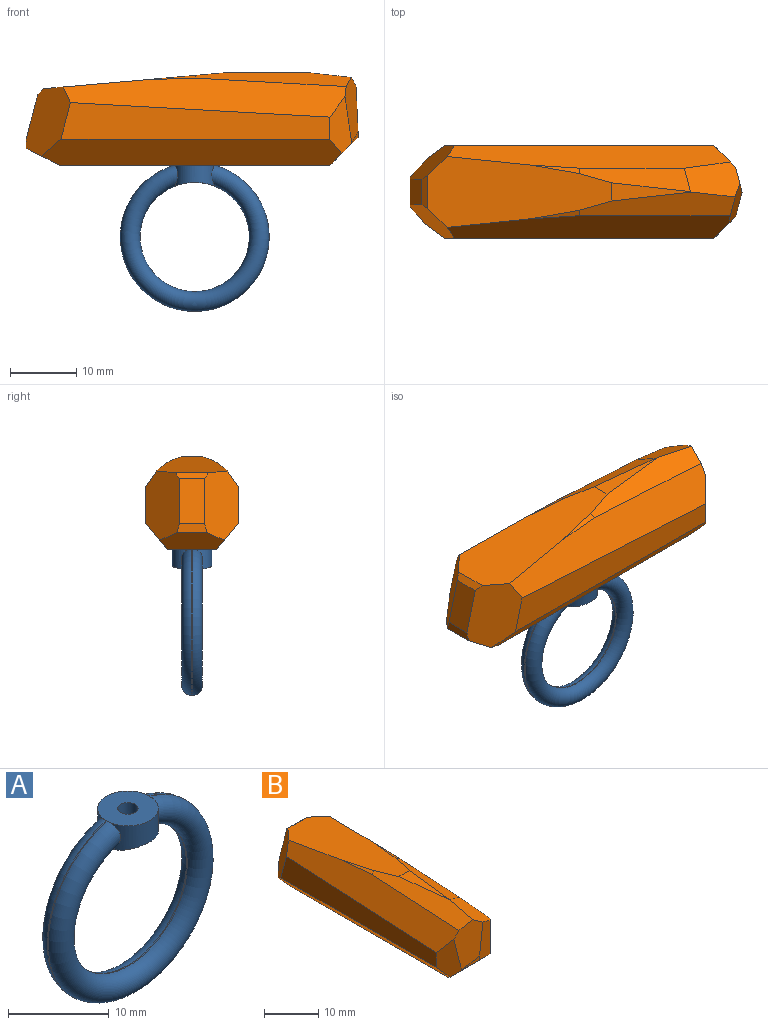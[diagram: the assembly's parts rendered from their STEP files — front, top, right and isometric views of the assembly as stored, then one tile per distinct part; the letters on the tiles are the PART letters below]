
ASSEMBLY  parts=2 mates=1
PART A: 8 faces, bbox 24.4x6x24 mm
  f0: cylinder r=11.25mm len=22.5mm, axis (0,1,0), area 7.9mm2, adj f1,f2,f4,f5,f6
  f1: cylinder r=3mm len=6mm, axis (0,0,-1), area 19mm2, adj f0,f3,f4,f6
  f2: cylinder r=3mm len=6mm, axis (0,0,-1), area 19mm2, adj f0,f3,f5,f6
  f3: cylinder r=8.25mm len=16.5mm, axis (0,1,0), area 31.2mm2, adj f1,f2,f4,f5,f7
  f4: torus R=9.75mm, axis (0,1,0), area 262.1mm2, adj f0,f1,f3
  f5: torus R=9.75mm, axis (0,1,0), area 262.1mm2, adj f0,f2,f3
  f6: plane 6x5.98mm, normal (0,0,1), area 25.1mm2, adj f0,f1,f2,f7
  f7: cylinder r=1mm len=2.66mm, axis (0,0,1), area 16.5mm2, adj f3,f6
PART B: 26 faces, bbox 14x50.2x14 mm
  f0: plane 40.84x7.43mm, normal (0,0,-1), area 303.5mm2, adj f3,f4,f24,f25
  f1: plane 40.65x5.53mm, normal (1,0,0), area 177.8mm2, adj f2,f5,f13,f25
  f2: plane 9.08x3.28mm, normal (0.71,-0.71,0), area 30.9mm2, adj f1,f3,f12,f13,f23,f25
  f3: plane 10.42x4.25mm, normal (0,-0.71,-0.71), area 46.6mm2, adj f0,f2,f12,f15,f19,f24,f25
  f4: plane 9.69x5.08mm, normal (0,0.45,-0.89), area 44.7mm2, adj f0,f5,f7,f16,f24,f25
  f5: plane 10.47x6.72mm, normal (0.71,0.68,0.18), area 66.6mm2, adj f1,f4,f7,f10,f11,f13,f21,f25
  f6: plane 12.11x2.75mm, normal (0,0,1), area 16.9mm2, adj f9,f18,f21,f23
  f7: plane 4.5x1.3mm, normal (0,1,0), area 5.4mm2, adj f4,f5,f11,f16
  f8: plane 7.26x1.27mm, normal (0.45,0,0.89), area 3.3mm2, adj f9,f13,f21
  f9: plane 16.79x3.55mm, normal (0.45,-0.05,0.89), area 44.9mm2, adj f6,f8,f13,f21,f23
  f10: plane 5.05x0.85mm, normal (0,0.71,0.71), area 5.3mm2, adj f5,f11,f16,f21
  f11: plane 6.88x3.84mm, normal (0,0.97,0.25), area 27.3mm2, adj f5,f7,f10,f16
  f12: plane 8.8x3.72mm, normal (0.25,-0.97,0), area 26.1mm2, adj f2,f3,f19,f22,f23
  f13: plane 42.76x5.89mm, normal (0.81,-0.03,0.58), area 211mm2, adj f1,f2,f5,f8,f9,f21,f23
  f14: plane 40.65x5.53mm, normal (-1,0,0), area 177.8mm2, adj f15,f16,f20,f24
  f15: plane 8.54x3.28mm, normal (-0.71,-0.71,0), area 25.5mm2, adj f3,f14,f19,f20,f22,f24
  f16: plane 10.47x6.72mm, normal (-0.71,0.68,0.18), area 66.6mm2, adj f4,f7,f10,f11,f14,f20,f21,f24
  f17: plane 7.26x1.27mm, normal (-0.45,0,0.89), area 3.3mm2, adj f18,f20,f21
  f18: plane 23.53x3.57mm, normal (-0.45,-0.05,0.89), area 69.8mm2, adj f6,f17,f20,f21,f22,f23
  f19: plane 3.72x1.88mm, normal (-0.25,-0.97,0), area 1.9mm2, adj f3,f12,f15,f22
  f20: plane 42.76x5.89mm, normal (-0.81,-0.03,0.58), area 216.5mm2, adj f14,f15,f16,f17,f18,f21,f22
  f21: plane 27.84x10.7mm, normal (0,0.09,1), area 213.5mm2, adj f5,f6,f8,f9,f10,f13,f16,f17
  f22: plane 9.9x5.93mm, normal (-0.29,-0.95,0.09), area 42mm2, adj f12,f15,f18,f19,f20,f23
  f23: plane 8.4x5.3mm, normal (0.46,-0.15,0.87), area 38.7mm2, adj f2,f6,f9,f12,f13,f18,f22
  f24: plane 45.34x3.93mm, normal (-0.77,0,-0.64), area 220.5mm2, adj f0,f3,f4,f14,f15,f16
  f25: plane 45.34x3.93mm, normal (0.77,0,-0.64), area 220.5mm2, adj f0,f1,f2,f3,f4,f5
PLACE A t=(53.47,26.41,-6.52)mm
PLACE B rot(axis=(0,0,1),90deg) t=(53.97,26.41,11.32)mm
MATE fastened B.f0 <-> A.f7  axis (0,0,-1) through (53.47,26.41,4.32)mm
